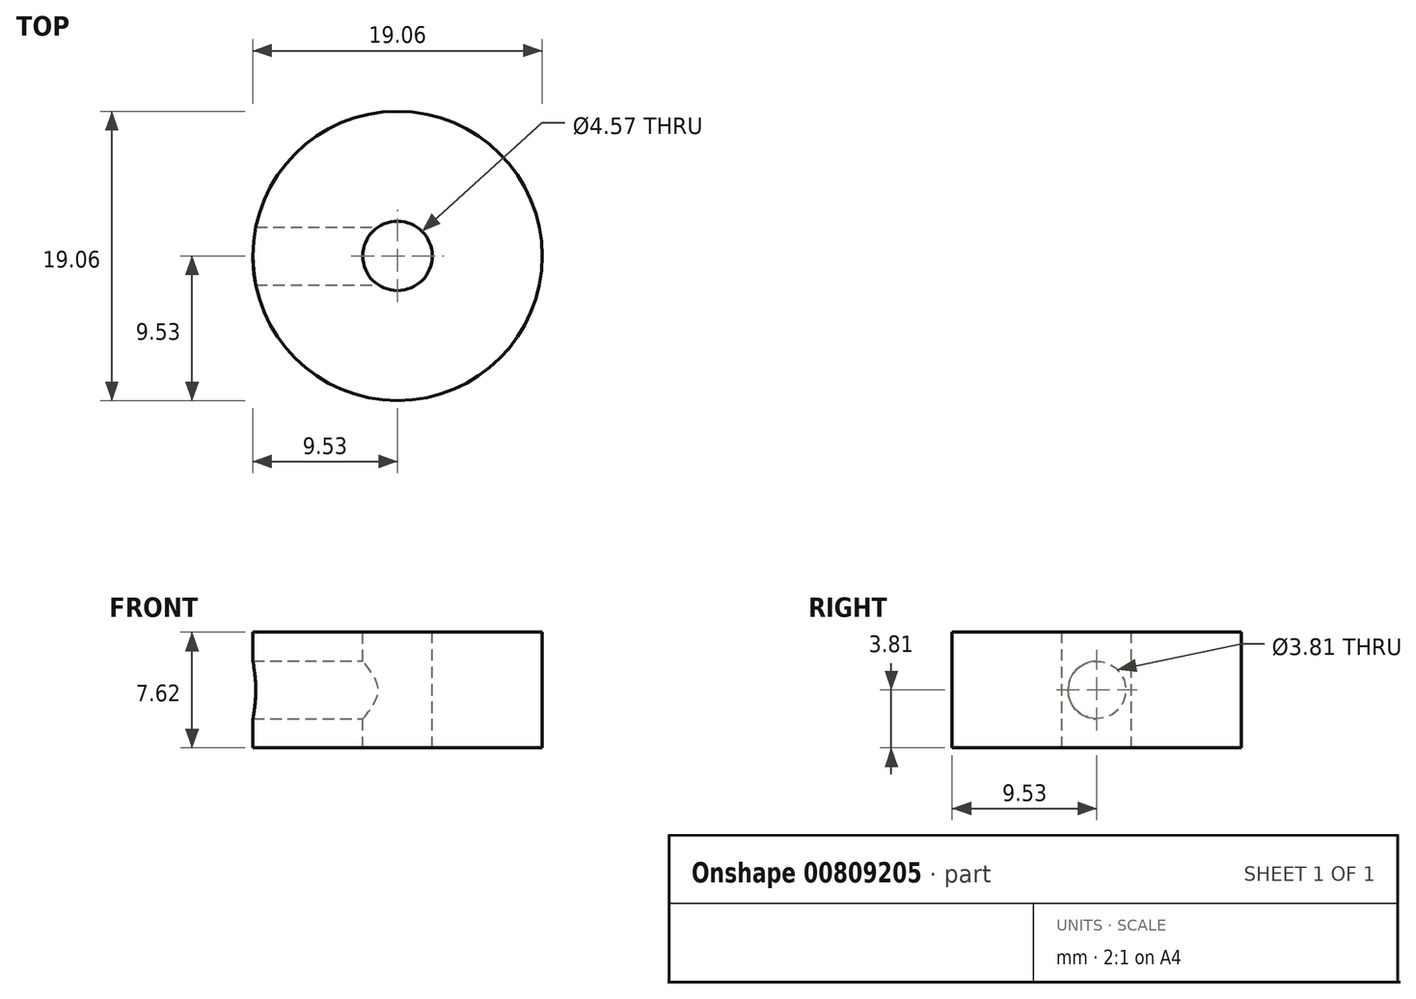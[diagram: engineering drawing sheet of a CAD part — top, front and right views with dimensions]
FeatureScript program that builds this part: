
annotation { "Feature Type Name" : "Feature", "Feature Type Description" : "" }
export const myFeature = defineFeature(function(context is Context, id is Id, definition is map)
    precondition{}
    {
        {
            var Q0;
            Q0=qCreatedBy(makeId("Top.planeOp"),FACE);
            var sketch = newSketch(context, id + "F0", { "sketchPlane" : qUnion([Q0])});
            skCircle(sketch, "E0", {"center": v(0, 0) * mm, "radius": 9.53 * mm});
            skSolve(sketch);
        }
        {
            var Q0;
            Q0=makeQuery(id+"F0.imprint","IMPRINT",FACE,{"disambiguationData":[TD([[makeQuery(id+"F0.imprint","IMPRINT",EDGE,{"derivedFrom":sQuery(id+"F0.wireOp",EDGE,"E0")}),1.0]])]});
            extrude(context, id + "F1", {"entities" : qUnion([Q0]), "depth" : 7.62 * mm, "offsetDistance" : 25.4 * mm});
        }
        {
            var Q0;
            Q0=makeQuery(id+"F1.opExtrude","CAP_FACE",FACE,{"disambiguationData":[OSD([sQuery(id+"F0.wireOp",EDGE,"E0")])],"isStart":false});
            var sketch = newSketch(context, id + "F2", { "sketchPlane" : qUnion([Q0])});
            skCircle(sketch, "E1", {"center": v(0, 0) * mm, "radius": 2.29 * mm});
            skSolve(sketch);
        }
        {
            var Q0;
            Q0=makeQuery(id+"F2.imprint","IMPRINT",FACE,{"disambiguationData":[TD([[makeQuery(id+"F2.imprint","IMPRINT",EDGE,{"derivedFrom":sQuery(id+"F2.wireOp",EDGE,"E1")}),1.0]])]});
            extrude(context, id + "F3", {"entities" : qUnion([Q0]), "operationType" : NewBodyOperationType.REMOVE, "oppositeDirection" : true, "depth" : 25.4 * mm, "offsetDistance" : 25.4 * mm});
        }
        {
            var Q0;
            Q0=qCreatedBy(makeId("Right.planeOp"),FACE);
            var sketch = newSketch(context, id + "F4", { "sketchPlane" : qUnion([Q0])});
            skCircle(sketch, "E2", {"center": v(0, 3.81) * mm, "radius": 1.9 * mm});
            skSolve(sketch);
        }
        {
            var Q0;
            Q0 = qSketchRegion(id + "F4", true);
            extrude(context, id + "F5", {"entities" : qUnion([Q0]), "operationType" : NewBodyOperationType.REMOVE, "oppositeDirection" : true, "depth" : 25.4 * mm, "offsetDistance" : 25.4 * mm});
        }
    });
